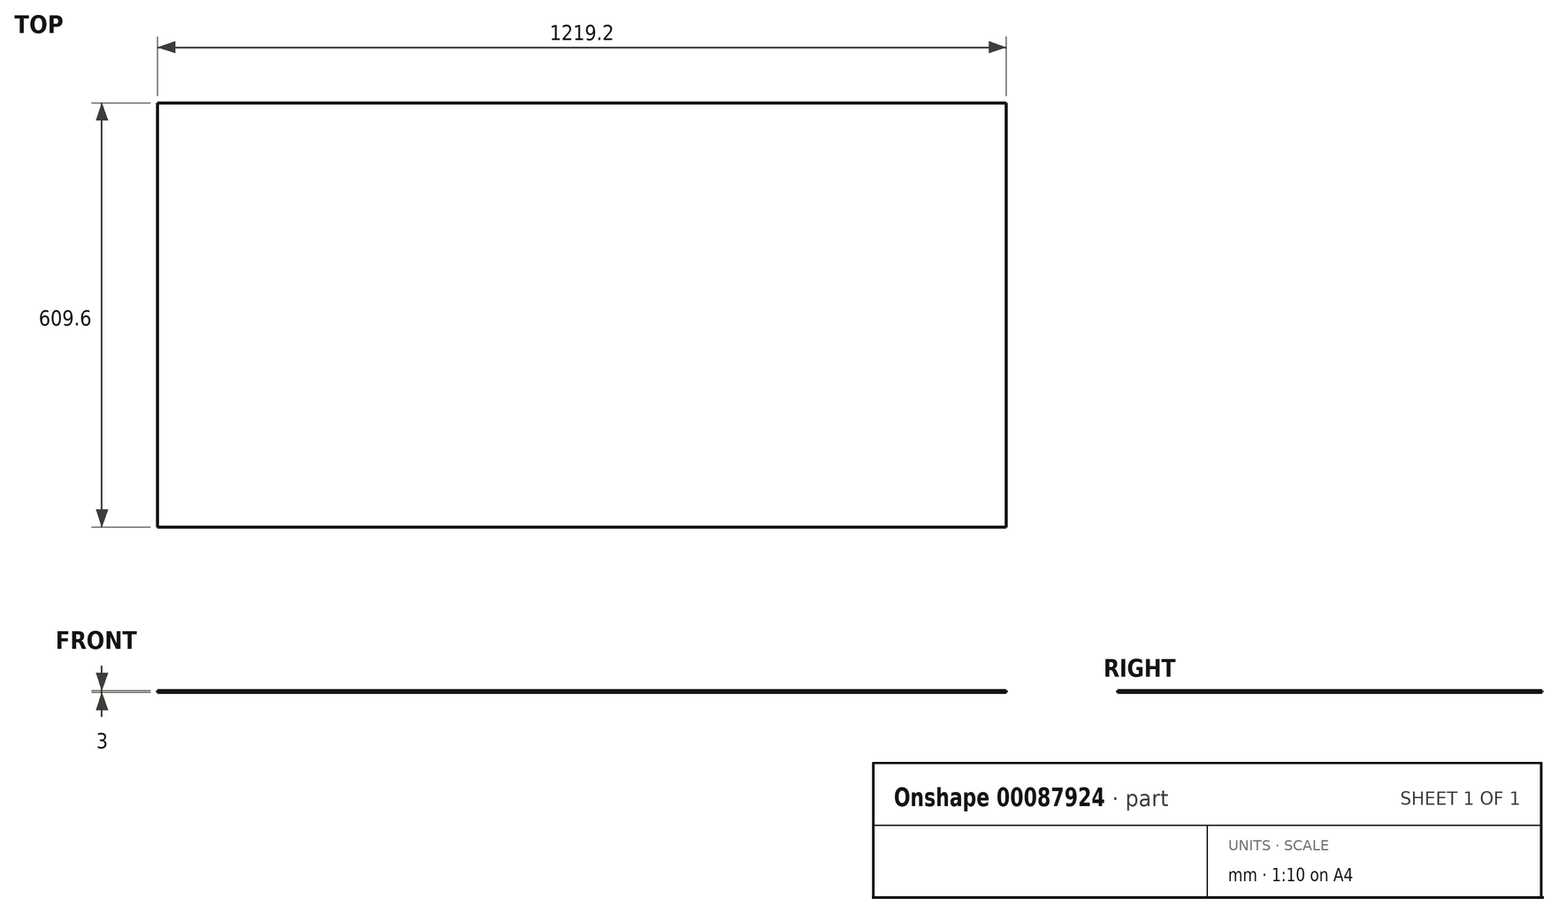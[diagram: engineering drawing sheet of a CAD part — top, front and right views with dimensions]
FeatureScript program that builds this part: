
annotation { "Feature Type Name" : "Feature", "Feature Type Description" : "" }
export const myFeature = defineFeature(function(context is Context, id is Id, definition is map)
    precondition{}
    {
        {
            var Q0;
            Q0=qCreatedBy(makeId("Top.planeOp"),FACE);
            var sketch = newSketch(context, id + "F0", { "sketchPlane" : qUnion([Q0])});
            skLineSegment(sketch, "E0.bottom", {"start": v(-609.6, -304.8) * mm, "end": v(609.6, -304.8) * mm});
            skLineSegment(sketch, "E0.top", {"start": v(-609.6, 304.8) * mm, "end": v(609.6, 304.8) * mm});
            skLineSegment(sketch, "E0.left", {"start": v(-609.6, -304.8) * mm, "end": v(-609.6, 304.8) * mm});
            skLineSegment(sketch, "E0.right", {"start": v(609.6, -304.8) * mm, "end": v(609.6, 304.8) * mm});
            skPoint(sketch, "E0.middle", {"position": v(0, 0) * mm});
            skSolve(sketch);
        }
        {
            var Q0;
            Q0=makeQuery(id+"F0.imprint","IMPRINT",FACE,{"disambiguationData":[TD([[makeQuery(id+"F0.imprint","IMPRINT",EDGE,{"derivedFrom":sQuery(id+"F0.wireOp",EDGE,"E0.bottom")}),1.0]])]});
            extrude(context, id + "F1", {"entities" : qUnion([Q0]), "depth" : 3 * mm});
        }
    });
